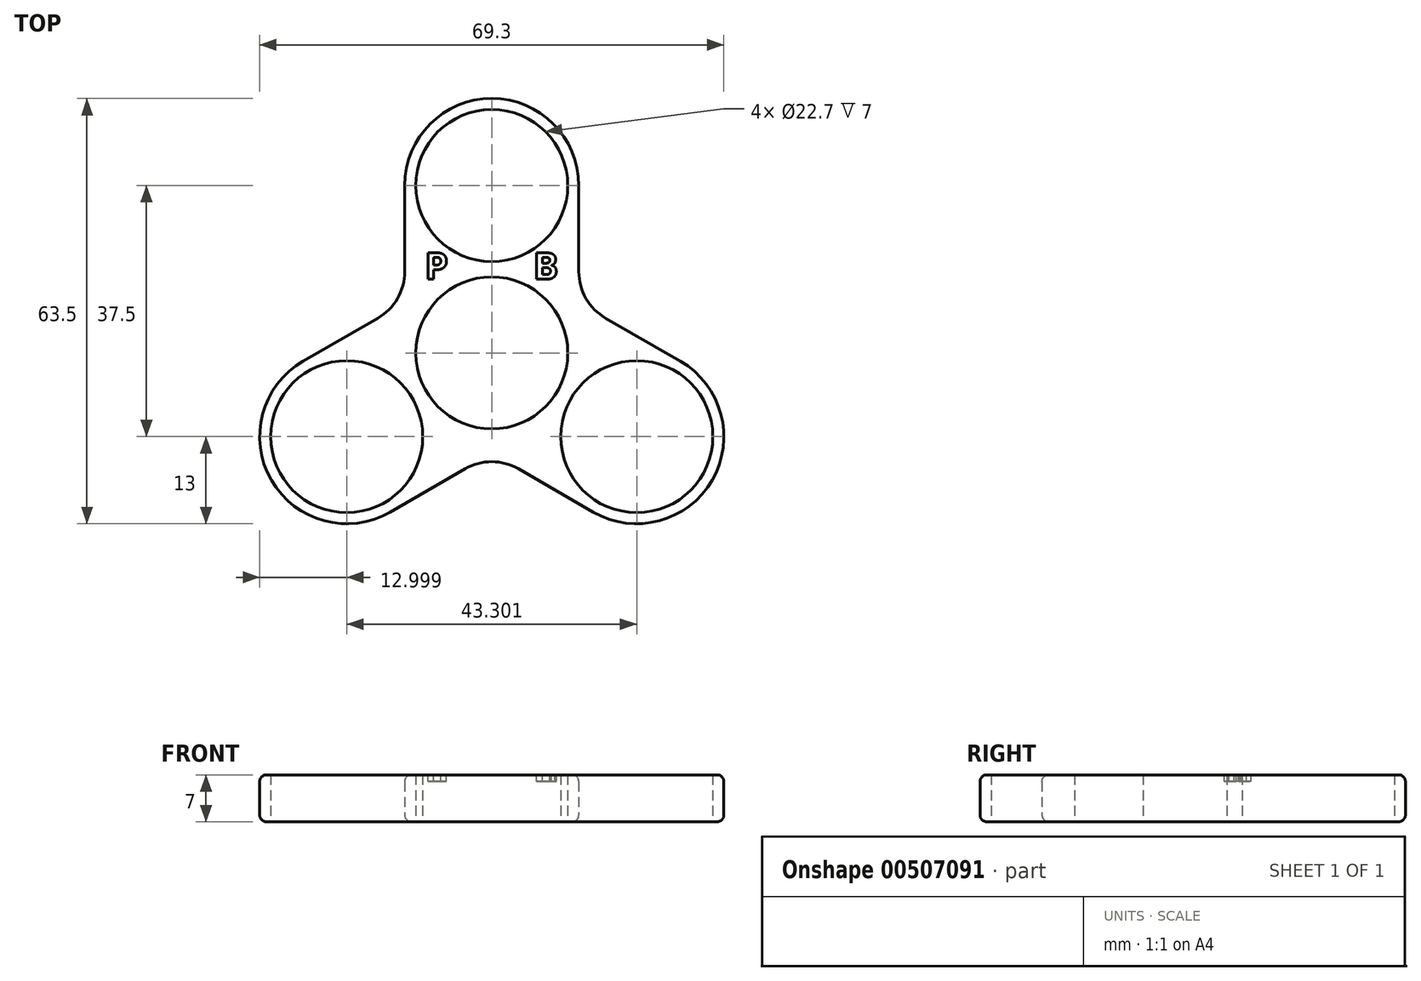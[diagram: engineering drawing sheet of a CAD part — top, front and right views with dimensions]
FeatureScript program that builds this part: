
annotation { "Feature Type Name" : "Feature", "Feature Type Description" : "" }
export const myFeature = defineFeature(function(context is Context, id is Id, definition is map)
    precondition{}
    {
        {
            var Q0;
            Q0=qCreatedBy(makeId("Top.planeOp"),FACE);
            var sketch = newSketch(context, id + "F0", { "sketchPlane" : qUnion([Q0])});
            skCircle(sketch, "E0", {"center": v(0, 0) * mm, "radius": 11.35 * mm});
            skCircle(sketch, "E1", {"center": v(21.65, -12.5) * mm, "radius": 11.35 * mm});
            skCircle(sketch, "E2", {"center": v(-21.65, -12.5) * mm, "radius": 11.35 * mm});
            skCircle(sketch, "E3", {"center": v(0, 25) * mm, "radius": 11.35 * mm});
            skLineSegment(sketch, "E4", {"start": v(0, 0) * mm, "end": v(0, 25) * mm, "construction": true});
            skLineSegment(sketch, "E5", {"start": v(0, 0) * mm, "end": v(21.65, -12.5) * mm, "construction": true});
            skLineSegment(sketch, "E6", {"start": v(0, 0) * mm, "end": v(-21.65, -12.5) * mm, "construction": true});
            skLineSegment(sketch, "E7", {"start": v(-17, 5.2) * mm, "end": v(-28.15, -1.24) * mm});
            skLineSegment(sketch, "E8", {"start": v(-15.15, -23.76) * mm, "end": v(-4, -17.32) * mm});
            skLineSegment(sketch, "E9", {"start": v(4, -17.32) * mm, "end": v(15.15, -23.76) * mm});
            skLineSegment(sketch, "E10", {"start": v(28.15, -1.24) * mm, "end": v(17, 5.2) * mm});
            skLineSegment(sketch, "E11", {"start": v(13, 12.12) * mm, "end": v(13, 25) * mm});
            skLineSegment(sketch, "E12", {"start": v(-13, 12.12) * mm, "end": v(-13, 25) * mm});
            skArc(sketch, "E13", {"start": v(-13, 25) * mm, "mid": v(0, 38) * mm, "end": v(13, 25) * mm});
            skArc(sketch, "E14", {"start": v(15.15, -23.76) * mm, "mid": v(32.9, -19) * mm, "end": v(28.15, -1.24) * mm});
            skArc(sketch, "E15", {"start": v(-15.15, -23.76) * mm, "mid": v(-32.9, -19) * mm, "end": v(-28.15, -1.24) * mm});
            skArc(sketch, "E16", {"start": v(-17, 5.2) * mm, "mid": v(-14.07, 8.12) * mm, "end": v(-13, 12.12) * mm});
            skArc(sketch, "E17", {"start": v(13, 12.12) * mm, "mid": v(14.07, 8.12) * mm, "end": v(17, 5.2) * mm});
            skArc(sketch, "E18", {"start": v(4, -17.32) * mm, "mid": v(0, -16.25) * mm, "end": v(-4, -17.32) * mm});
            skSolve(sketch);
        }
        {
            var Q0;
            Q0=makeQuery(id+"F0.imprint","IMPRINT",FACE,{"disambiguationData":[TD([[makeQuery(id+"F0.imprint","IMPRINT",EDGE,{"derivedFrom":sQuery(id+"F0.wireOp",EDGE,"E0")}),-1.0]])]});
            extrude(context, id + "F1", {"entities" : qUnion([Q0]), "depth" : 7 * mm});
        }
        {
            var Q0;
            Q0=makeQuery(id+"F1.opExtrude","CAP_EDGE",EDGE,{"disambiguationData":[OSD([sQuery(id+"F0.wireOp",EDGE,"E16")])],"isStart":false});
            var Q1;
            Q1=makeQuery(id+"F1.opExtrude","CAP_EDGE",EDGE,{"disambiguationData":[OSD([sQuery(id+"F0.wireOp",EDGE,"E16")])],"isStart":true});
            fillet(context, id + "F2", {"entities" : qUnion([Q0, Q1]), "radius" : 1 * mm, "tangentPropagation" : true, "allowEdgeOverflow" : false});
        }
        {
            var Q0;
            Q0=makeQuery(id+"F1.opExtrude","CAP_FACE",FACE,{"disambiguationData":[OSD([sQuery(id+"F0.wireOp",EDGE,"E0"),sQuery(id+"F0.wireOp",EDGE,"E1"),sQuery(id+"F0.wireOp",EDGE,"E2"),sQuery(id+"F0.wireOp",EDGE,"E3"),sQuery(id+"F0.wireOp",EDGE,"E7"),sQuery(id+"F0.wireOp",EDGE,"E8"),sQuery(id+"F0.wireOp",EDGE,"E9"),sQuery(id+"F0.wireOp",EDGE,"E10"),sQuery(id+"F0.wireOp",EDGE,"E11"),sQuery(id+"F0.wireOp",EDGE,"E12"),sQuery(id+"F0.wireOp",EDGE,"E13"),sQuery(id+"F0.wireOp",EDGE,"E14"),sQuery(id+"F0.wireOp",EDGE,"E15"),sQuery(id+"F0.wireOp",EDGE,"E16"),sQuery(id+"F0.wireOp",EDGE,"E17"),sQuery(id+"F0.wireOp",EDGE,"E18")])],"isStart":false});
            var sketch = newSketch(context, id + "F3", { "sketchPlane" : qUnion([Q0])});
            skText(sketch, "E19", { "text": "P", "fontName": "OpenSans-Bold.ttf"});
            skText(sketch, "E20", { "text": "B", "fontName": "OpenSans-Bold.ttf"});
            skLineSegment(sketch, "E21", {"start": v(6.2, 11.35) * mm, "end": v(-6.4, 11.35) * mm, "construction": true});
            skLineSegment(sketch, "E22", {"start": v(-6.4, 15.35) * mm, "end": v(6.2, 15.35) * mm, "construction": true});
            const initialGuessF3  = {"E19": [-0.01, 0.011, 1, 0, 0.004], "E20": [0.0062, 0.011, 1, 0, 0.004]};
            skSetInitialGuess(sketch, initialGuessF3);
            skSolve(sketch);
        }
        {
            var Q0;
            Q0 = qSketchRegion(id + "F3", true);
            extrude(context, id + "F4", {"entities" : qUnion([Q0]), "operationType" : NewBodyOperationType.REMOVE, "oppositeDirection" : true, "depth" : 1 * mm});
        }
    });
